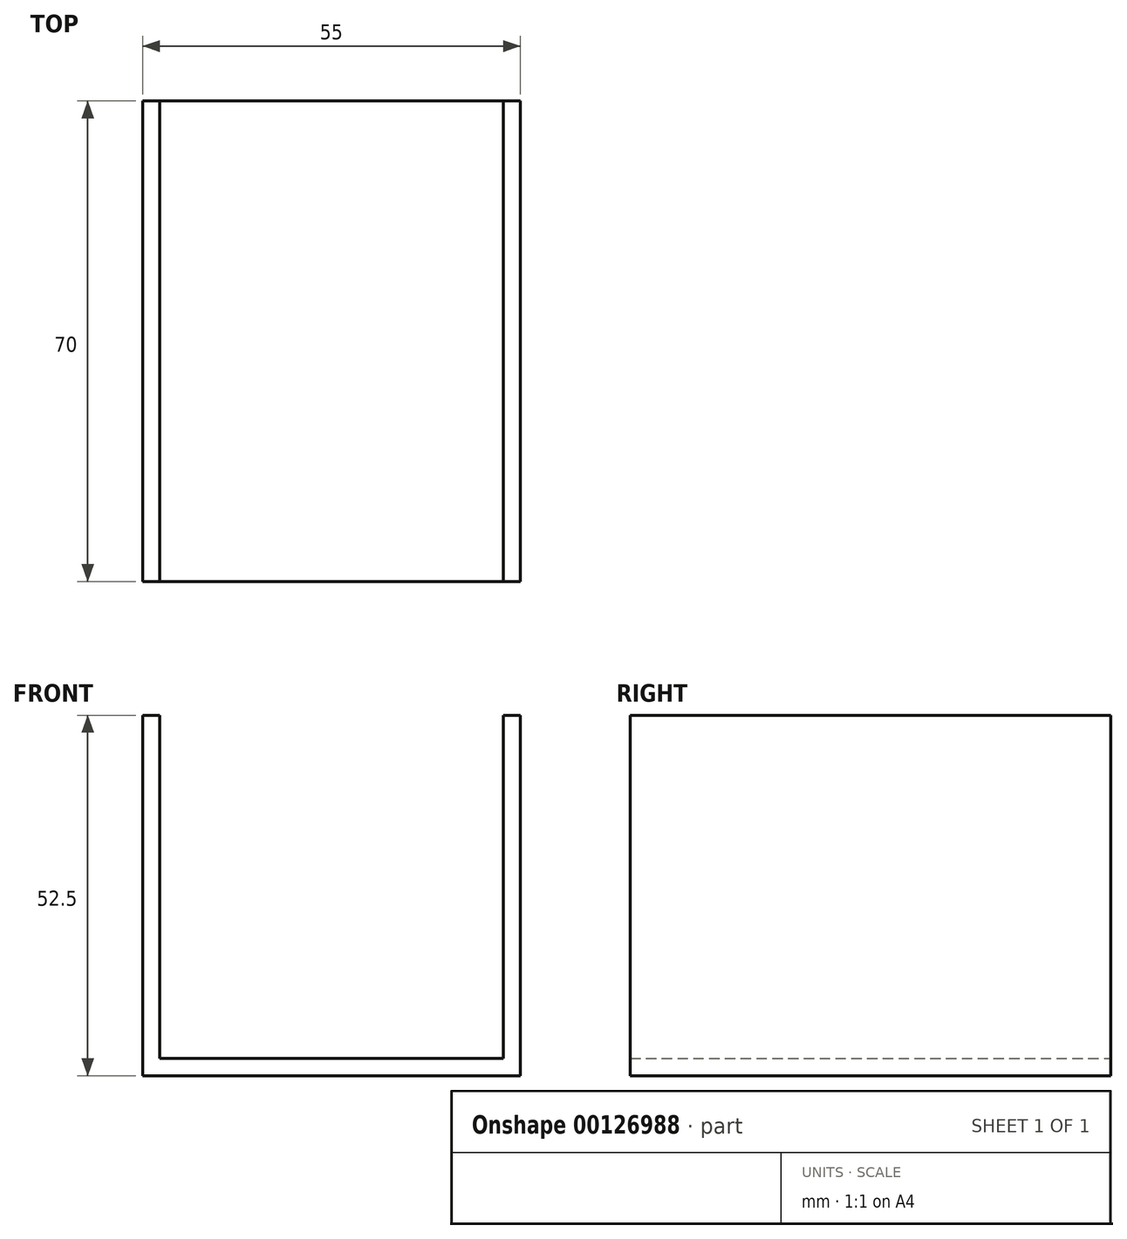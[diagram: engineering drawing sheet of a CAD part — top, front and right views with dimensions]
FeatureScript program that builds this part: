
annotation { "Feature Type Name" : "Feature", "Feature Type Description" : "" }
export const myFeature = defineFeature(function(context is Context, id is Id, definition is map)
    precondition{}
    {
        {
            var Q0;
            Q0=qCreatedBy(makeId("Front.planeOp"),FACE);
            var sketch = newSketch(context, id + "F0", { "sketchPlane" : qUnion([Q0])});
            skLineSegment(sketch, "E0.bottom", {"start": v(0, 0) * mm, "end": v(55, 0) * mm});
            skLineSegment(sketch, "E0.left", {"start": v(0, 0) * mm, "end": v(0, 52.5) * mm});
            skLineSegment(sketch, "E0.right", {"start": v(55, 0) * mm, "end": v(55, 52.5) * mm});
            skPoint(sketch, "E0.middle", {"position": v(27.5, 27.5) * mm});
            skLineSegment(sketch, "E1.bottom", {"start": v(2.5, 2.5) * mm, "end": v(52.5, 2.5) * mm});
            skLineSegment(sketch, "E1.left", {"start": v(2.5, 2.5) * mm, "end": v(2.5, 52.5) * mm});
            skLineSegment(sketch, "E1.right", {"start": v(52.5, 2.5) * mm, "end": v(52.5, 52.5) * mm});
            skLineSegment(sketch, "E2", {"start": v(2.5, 52.5) * mm, "end": v(0, 52.5) * mm});
            skLineSegment(sketch, "E3", {"start": v(52.5, 52.5) * mm, "end": v(55, 52.5) * mm});
            skPoint(sketch, "E4.orphan", {"position": v(0, 55) * mm});
            skPoint(sketch, "E5.orphan", {"position": v(55, 55) * mm});
            skSolve(sketch);
        }
        {
            var Q0;
            Q0 = qSketchRegion(id + "F0", true);
            extrude(context, id + "F1", {"entities" : qUnion([Q0]), "depth" : 70 * mm});
        }
    });
